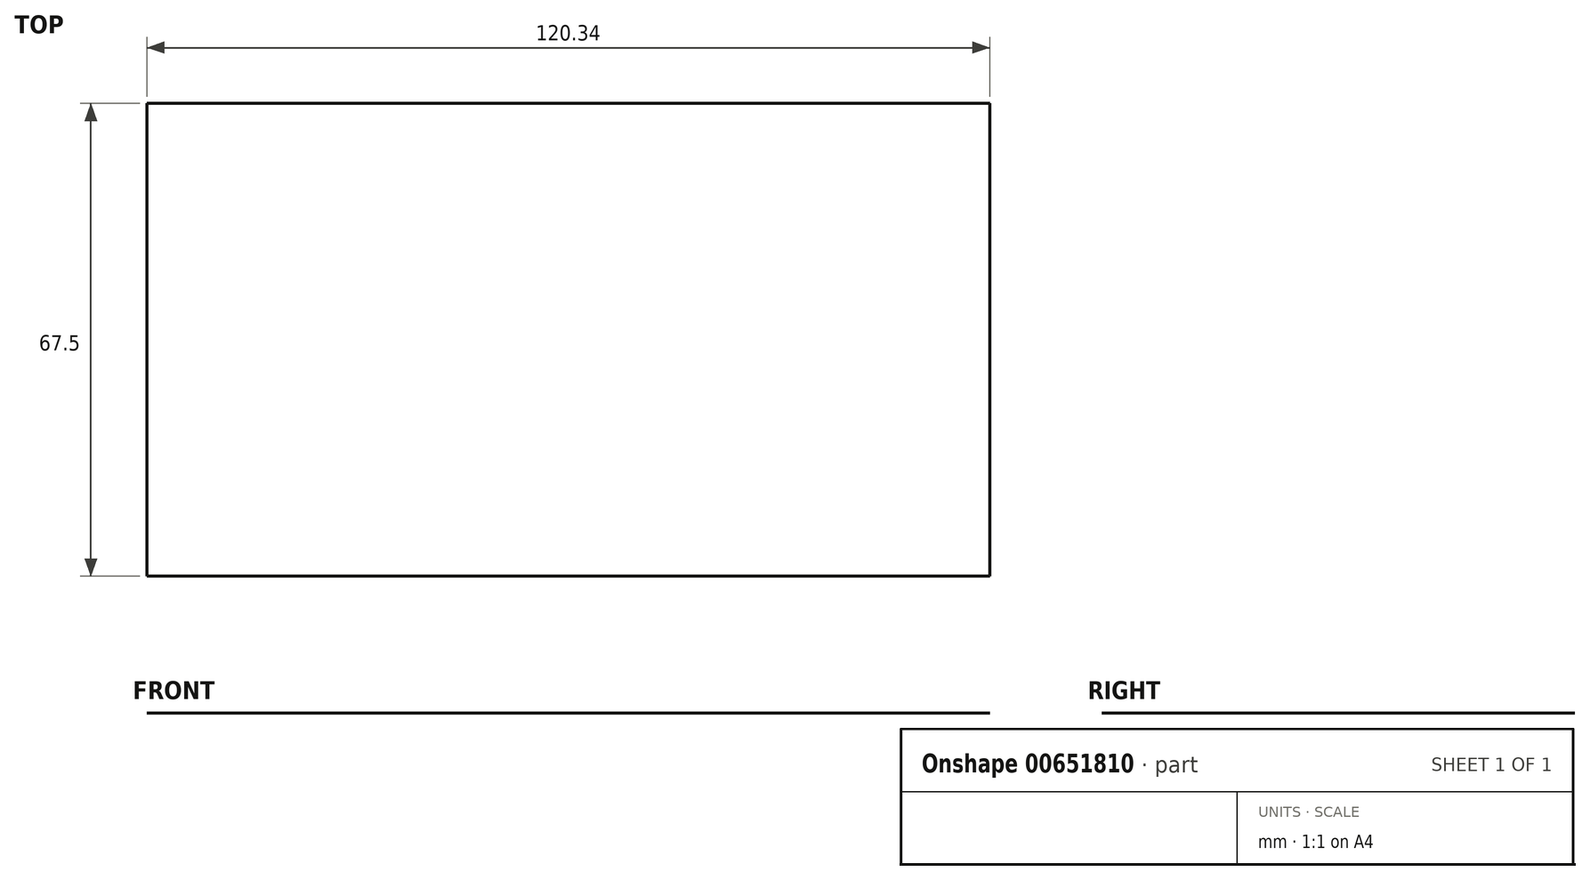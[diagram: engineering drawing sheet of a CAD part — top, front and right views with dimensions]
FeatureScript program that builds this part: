
annotation { "Feature Type Name" : "Feature", "Feature Type Description" : "" }
export const myFeature = defineFeature(function(context is Context, id is Id, definition is map)
    precondition{}
    {
        {
            var Q0;
            Q0=qCreatedBy(makeId("Front.planeOp"),FACE);
            var sketch = newSketch(context, id + "F0", { "sketchPlane" : qUnion([Q0])});
            skLineSegment(sketch, "E0.bottom", {"start": v(60.17, 1.13) * mm, "end": v(-60.17, 1.13) * mm});
            skLineSegment(sketch, "E0.top", {"start": v(60.17, -1.13) * mm, "end": v(-60.17, -1.13) * mm});
            skLineSegment(sketch, "E0.left", {"start": v(60.17, 1.13) * mm, "end": v(60.17, -1.13) * mm});
            skLineSegment(sketch, "E0.right", {"start": v(-60.17, 1.13) * mm, "end": v(-60.17, -1.13) * mm});
            skPoint(sketch, "E0.middle", {"position": v(0, 0) * mm});
            skSolve(sketch);
        }
        {
            var Q0;
            Q0=sQuery(id+"F0.wireOp",EDGE,"E0.top");
            extrude(context, id + "F1", {"bodyType" : ToolBodyType.SURFACE, "surfaceEntities" : qUnion([Q0]), "depth" : 67.5 * mm, "offsetDistance" : 25.4 * mm});
        }
    });
